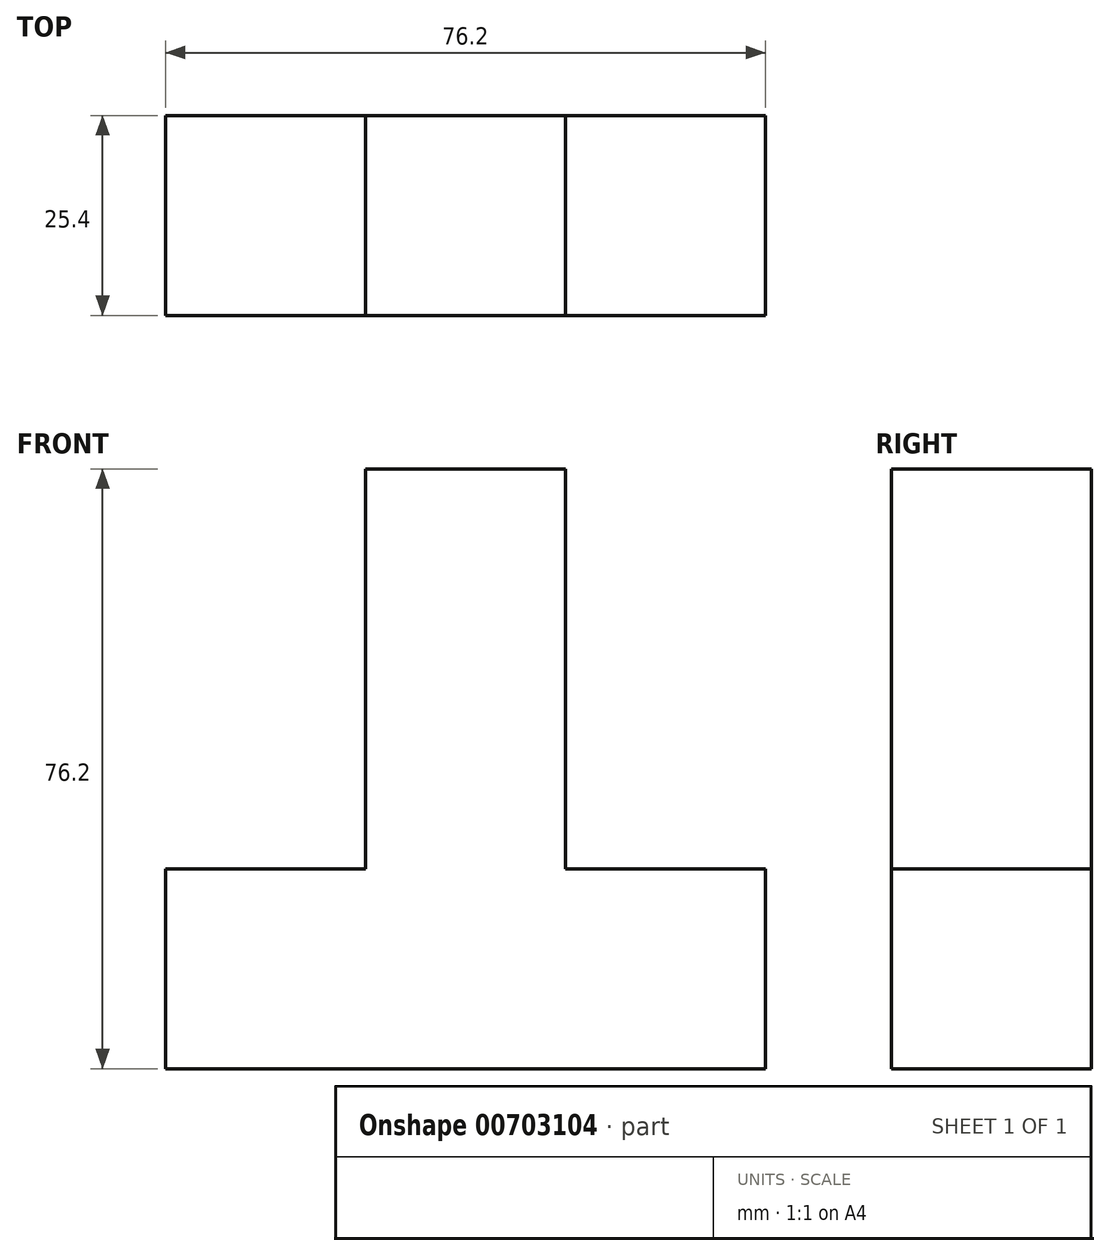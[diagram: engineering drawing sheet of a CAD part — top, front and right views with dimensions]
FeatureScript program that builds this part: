
annotation { "Feature Type Name" : "Feature", "Feature Type Description" : "" }
export const myFeature = defineFeature(function(context is Context, id is Id, definition is map)
    precondition{}
    {
        {
            var Q0;
            Q0=qCreatedBy(makeId("Front.planeOp"),FACE);
            var sketch = newSketch(context, id + "F0", { "sketchPlane" : qUnion([Q0])});
            skLineSegment(sketch, "E0", {"start": v(-43.83, -1.24) * mm, "end": v(32.37, -1.24) * mm});
            skLineSegment(sketch, "E1", {"start": v(32.37, -1.24) * mm, "end": v(32.37, 24.16) * mm});
            skLineSegment(sketch, "E2", {"start": v(32.37, 24.16) * mm, "end": v(6.97, 24.16) * mm});
            skLineSegment(sketch, "E3", {"start": v(6.97, 24.16) * mm, "end": v(6.97, 74.96) * mm});
            skLineSegment(sketch, "E4", {"start": v(6.97, 74.96) * mm, "end": v(-18.43, 74.96) * mm});
            skLineSegment(sketch, "E5", {"start": v(-18.43, 74.96) * mm, "end": v(-18.43, 24.16) * mm});
            skLineSegment(sketch, "E6", {"start": v(-18.43, 24.16) * mm, "end": v(-43.83, 24.16) * mm});
            skLineSegment(sketch, "E7", {"start": v(-43.83, 24.16) * mm, "end": v(-43.83, -1.24) * mm});
            skSolve(sketch);
        }
        {
            var Q0;
            Q0=makeQuery(id+"F0.imprint","IMPRINT",FACE,{"disambiguationData":[TD([[makeQuery(id+"F0.imprint","IMPRINT",EDGE,{"derivedFrom":sQuery(id+"F0.wireOp",EDGE,"E0")}),1.0]])]});
            extrude(context, id + "F1", {"entities" : qUnion([Q0]), "depth" : 25.4 * mm, "offsetDistance" : 25.4 * mm});
        }
    });
